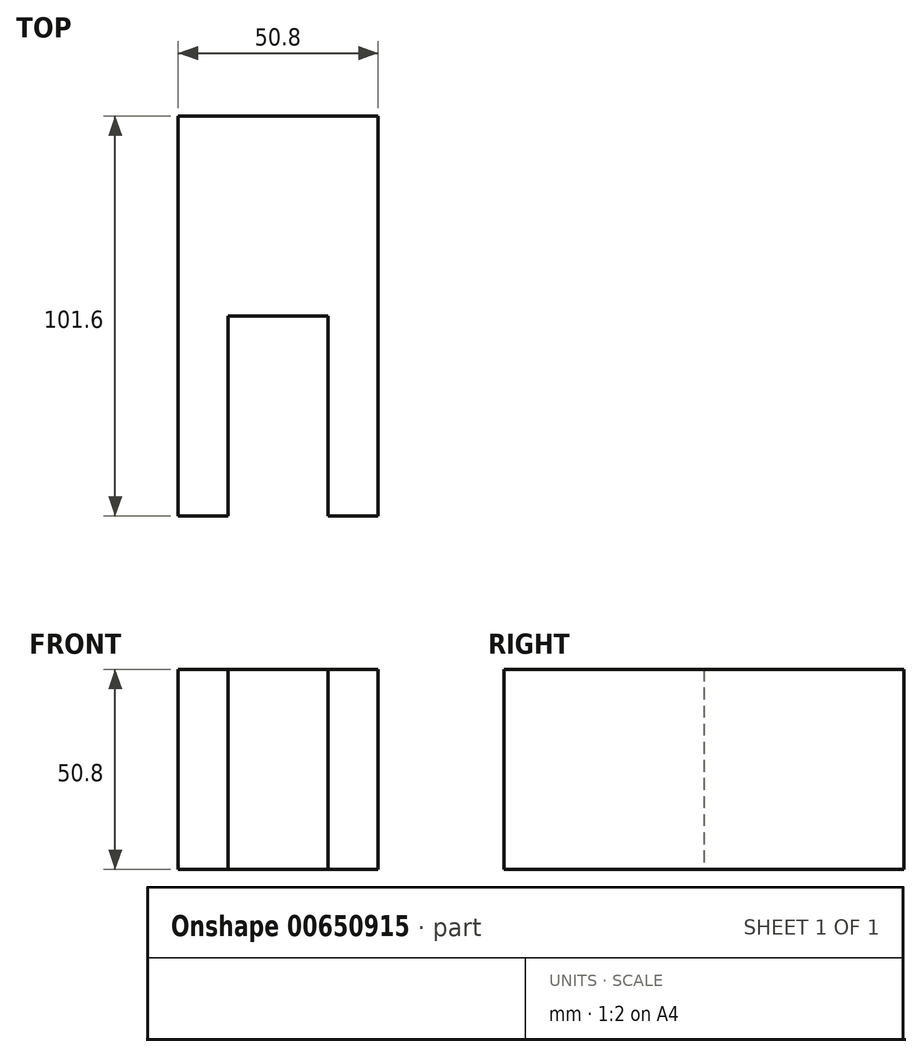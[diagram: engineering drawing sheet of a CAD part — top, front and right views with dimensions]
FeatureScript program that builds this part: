
annotation { "Feature Type Name" : "Feature", "Feature Type Description" : "" }
export const myFeature = defineFeature(function(context is Context, id is Id, definition is map)
    precondition{}
    {
        {
            var Q0;
            Q0=qCreatedBy(makeId("Top.planeOp"),FACE);
            var sketch = newSketch(context, id + "F0", { "sketchPlane" : qUnion([Q0])});
            skLineSegment(sketch, "E0.bottom", {"start": v(-25.4, 50.8) * mm, "end": v(25.4, 50.8) * mm});
            skLineSegment(sketch, "E0.top", {"start": v(-25.4, -50.8) * mm, "end": v(25.4, -50.8) * mm});
            skLineSegment(sketch, "E0.left", {"start": v(-25.4, 50.8) * mm, "end": v(-25.4, -50.8) * mm});
            skLineSegment(sketch, "E0.right", {"start": v(25.4, 50.8) * mm, "end": v(25.4, -50.8) * mm});
            skPoint(sketch, "E0.middle", {"position": v(0, 0) * mm});
            skPoint(sketch, "E1", {"position": v(0, -50.8) * mm});
            skPoint(sketch, "E2", {"position": v(-12.7, -50.8) * mm});
            skPoint(sketch, "E3", {"position": v(12.7, -50.8) * mm});
            skLineSegment(sketch, "E4.bottom", {"start": v(-12.7, -50.8) * mm, "end": v(12.7, -50.8) * mm});
            skLineSegment(sketch, "E4.top", {"start": v(-12.7, 0) * mm, "end": v(12.7, 0) * mm});
            skLineSegment(sketch, "E4.left", {"start": v(-12.7, -50.8) * mm, "end": v(-12.7, 0) * mm});
            skLineSegment(sketch, "E4.right", {"start": v(12.7, -50.8) * mm, "end": v(12.7, 0) * mm});
            skSolve(sketch);
        }
        {
            var Q0;
            Q0=makeQuery(id+"F0.imprint","IMPRINT",FACE,{"disambiguationData":[TD([[makeQuery(id+"F0.imprint","IMPRINT",EDGE,{"derivedFrom":sQuery(id+"F0.wireOp",EDGE,"E0.bottom")}),-1.0]])]});
            extrude(context, id + "F1", {"entities" : qUnion([Q0]), "depth" : 50.8 * mm, "offsetDistance" : 25.4 * mm});
        }
    });
